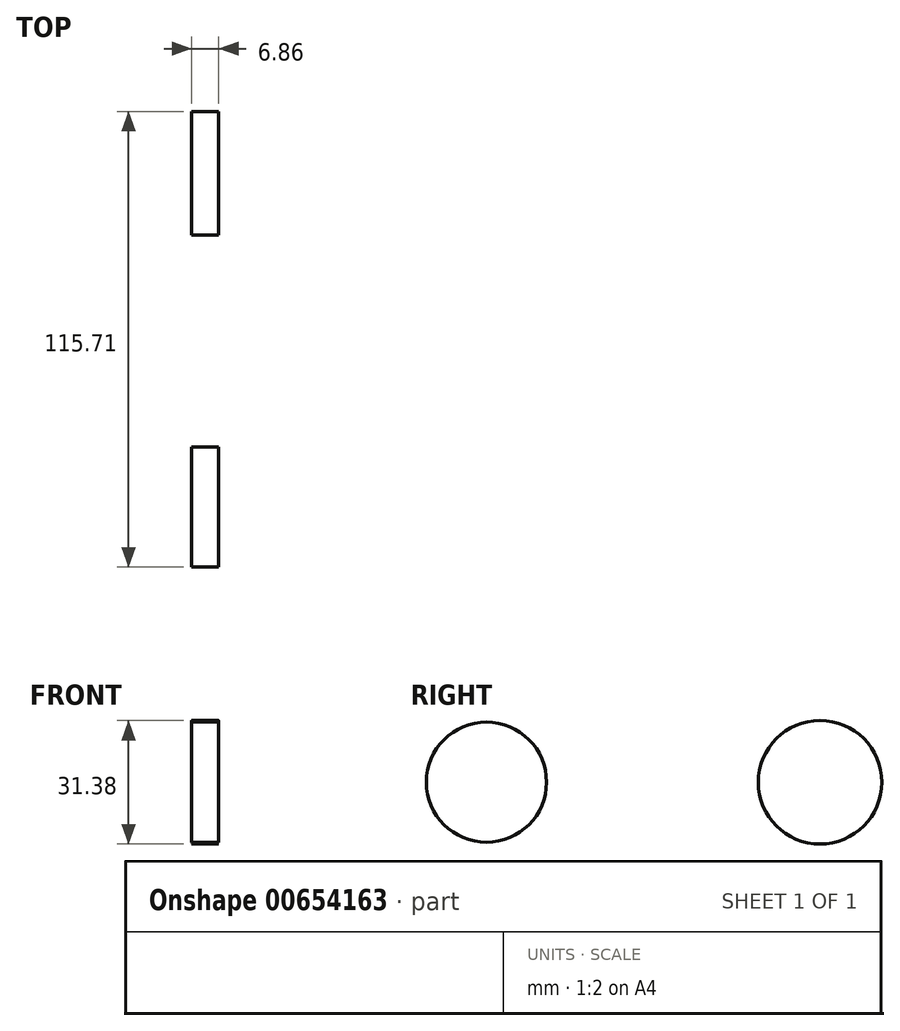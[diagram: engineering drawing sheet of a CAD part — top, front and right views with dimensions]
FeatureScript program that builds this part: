
annotation { "Feature Type Name" : "Feature", "Feature Type Description" : "" }
export const myFeature = defineFeature(function(context is Context, id is Id, definition is map)
    precondition{}
    {
        {
            var Q0;
            Q0=qCreatedBy(makeId("Right.planeOp"),FACE);
            var sketch = newSketch(context, id + "F0", { "sketchPlane" : qUnion([Q0])});
            skCircle(sketch, "E0", {"center": v(-53.18, 15.45) * mm, "radius": 15.27 * mm});
            skCircle(sketch, "E1", {"center": v(31.57, 15.45) * mm, "radius": 15.7 * mm});
            skSolve(sketch);
        }
        {
            var Q0;
            Q0=makeQuery(id+"F0.imprint","IMPRINT",FACE,{"disambiguationData":[TD([[makeQuery(id+"F0.imprint","IMPRINT",EDGE,{"derivedFrom":sQuery(id+"F0.wireOp",EDGE,"E0")}),1.0]])]});
            var sketch = newSketch(context, id + "F1", { "sketchPlane" : qUnion([Q0])});
            skSolve(sketch);
        }
        {
            var Q0;
            Q0 = qSketchRegion(id + "F1", true);
            var Q1;
            Q1=makeQuery(id+"F1.imprint","IMPRINT",FACE,{"disambiguationData":[TD([[makeQuery(id+"F1.imprint","IMPRINT",EDGE,{"derivedFrom":makeQuery(id+"F0.imprint","IMPRINT",EDGE,{"derivedFrom":sQuery(id+"F0.wireOp",EDGE,"E0")})}),1.0]])]});
            extrude(context, id + "F2", {"entities" : qUnion([Q0, Q1]), "depth" : 6.86 * mm, "offsetDistance" : 25.4 * mm});
        }
        {
            var Q0;
            Q0=makeQuery(id+"F0.imprint","IMPRINT",FACE,{"disambiguationData":[TD([[makeQuery(id+"F0.imprint","IMPRINT",EDGE,{"derivedFrom":sQuery(id+"F0.wireOp",EDGE,"E1")}),1.0]])]});
            var sketch = newSketch(context, id + "F3", { "sketchPlane" : qUnion([Q0])});
            skSolve(sketch);
        }
        {
            var Q0;
            Q0 = qSketchRegion(id + "F3", true);
            var Q1;
            Q1=makeQuery(id+"F3.imprint","IMPRINT",FACE,{"disambiguationData":[TD([[makeQuery(id+"F3.imprint","IMPRINT",EDGE,{"derivedFrom":makeQuery(id+"F0.imprint","IMPRINT",EDGE,{"derivedFrom":sQuery(id+"F0.wireOp",EDGE,"E1")})}),1.0]])]});
            extrude(context, id + "F4", {"entities" : qUnion([Q0, Q1]), "depth" : 6.86 * mm, "offsetDistance" : 25.4 * mm});
        }
        {
            var Q0;
            Q0=qCreatedBy(makeId("Right.planeOp"),FACE);
            var sketch = newSketch(context, id + "F5", { "sketchPlane" : qUnion([Q0])});
            skLineSegment(sketch, "E2", {"start": v(-52.42, 15.26) * mm, "end": v(-26.26, 15.26) * mm});
            skLineSegment(sketch, "E3", {"start": v(-52.42, 15.26) * mm, "end": v(-26.26, 36.3) * mm});
            skLineSegment(sketch, "E4", {"start": v(-26.26, 15.26) * mm, "end": v(-26.26, 36.3) * mm});
            skLineSegment(sketch, "E5", {"start": v(-26.26, 15.26) * mm, "end": v(28.72, 47.68) * mm});
            skLineSegment(sketch, "E6", {"start": v(-26.26, 36.3) * mm, "end": v(28.72, 47.68) * mm});
            skLineSegment(sketch, "E7", {"start": v(28.72, 47.68) * mm, "end": v(31.57, 15.26) * mm});
            skCircle(sketch, "E8", {"center": v(-26.26, 15.26) * mm, "radius": 2.65 * mm});
            skSolve(sketch);
        }
        {
            var Q0;
            Q0=makeQuery(id+"F2.opExtrude","CAP_FACE",FACE,{"disambiguationData":[OSD([sQuery(id+"F0.wireOp",EDGE,"E0")])],"isStart":false});
            var sketch = newSketch(context, id + "F6", { "sketchPlane" : qUnion([Q0])});
            skLineSegment(sketch, "E9", {"start": v(-53.18, 15.45) * mm, "end": v(-26.45, 15.45) * mm});
            skLineSegment(sketch, "E10", {"start": v(-26.45, 15.45) * mm, "end": v(-26.45, 36.5) * mm});
            skLineSegment(sketch, "E11", {"start": v(-26.45, 36.5) * mm, "end": v(-53.18, 15.45) * mm});
            skLineSegment(sketch, "E12", {"start": v(-26.45, 36.5) * mm, "end": v(28.72, 47.87) * mm});
            skLineSegment(sketch, "E13", {"start": v(28.72, 47.87) * mm, "end": v(-26.45, 15.45) * mm});
            skLineSegment(sketch, "E14", {"start": v(28.72, 47.87) * mm, "end": v(31.57, 15.45) * mm});
            skCircle(sketch, "E15", {"center": v(-26.45, 15.45) * mm, "radius": 3.03 * mm});
            skSolve(sketch);
        }
        {
            var Q0;
            Q0=sQuery(id+"F6.wireOp",VERTEX,"E12.end");
            var Q1;
            Q1=sQuery(id+"F5.wireOp",VERTEX,"E7.start");
            var Q2;
            Q2=sQuery(id+"F5.wireOp",VERTEX,"E7.end");
            cPlane(context, id + "F7", {"entities" : qUnion([Q0, Q1, Q2]), "cplaneType" : CPlaneType.THREE_POINT, "offset" : 25.4 * mm, "width" : 152.4 * mm, "height" : 152.4 * mm});
        }
    });
